# Revit family: Dauphin-Bosse S2_Telephone Booth
name_source: partatom
category: Casework
units: mm (PartAtom-declared; Revit-internal decimal feet)

## family parameters
Always vertical = Yes
Cut with Voids When Loaded = No
Room Calculation Point = No
Shared = No
Work Plane-Based = No

## types (3) — shared parameters
Depth = 1248 mm  [stored 4.09449 ft]
Description = Bosse Telephone Booth
Door Handle Material = Bosse_Door Handle Material
Door Metal Material = Bosse_Door Metal Material
Height = 2400 mm
Manufacturer = Dauphin North America
Model = BP2T_P47X49X94
Panel Exterior Material = Bosse_Panel Exterior Material
Panel Glass Material = Bosse_Panel Glass Material
Panel Left Interior Finish = Bosse_Fabric Divina Asphalt Grey
Panel Right Interior Material = Bosse_Fabric Divina Asphalt Grey
Panel Top_Bottom Interior Finish = Bosse_Fabric Divina Asphalt Grey
Panel_Side_Depth = 1169 mm  [stored 3.8353 ft]
Shelf Break Material = Bosse_Shelf Break Material
Shelf Main Material = Bosse_Shelf Main Material
Type Comments = Bosse S2 Telepophone Booth PURE
URL = www.dauphin.co.za
Width = 1210 mm  [stored 3.96982 ft]

## per-type parameters (varying)
| type | Shelf Left | Shelf Right |
| BP2T_P47X49X94 - Telephone Cube no Shelf | No | No |
| BP2T_P47X49X94 - Telephone Cube Shelf Left | Yes | No |
| BP2T_P47X49X94 - Telephone Cube Shelf Right | No | Yes |

note: [stored X ft] marks values corroborated as IEEE doubles in the binary element streams (Revit-internal decimal feet)

## geometry (parser evidence)
native form markers: Sweep x22
no freeform markers — native parametric forms only
